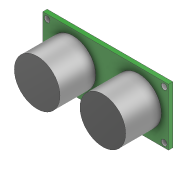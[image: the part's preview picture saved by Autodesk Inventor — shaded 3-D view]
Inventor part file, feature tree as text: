
AUTODESK INVENTOR PART (.ipt)
format: ipt  version: 2022 (Build 260153000, 153)  size: 144,384 bytes
history: native  units: mm
features: sketch x3, extrude x2, hole x1
ambient origin geometry x8: Origin, YZ Plane, XZ Plane, XY Plane, X Axis, Y Axis, Z Axis, Center Point
bodies: Solid1 (feature_tree)
feature tree (6):
  extrude  "Extrusion1"  Depth=20.0mm
  extrude  "Extrusion2"  Depth=1.5mm
  hole  "Hole1"  [1 undecoded]
  sketch  "Sketch1"  dims[d0=44.0mm d1=20.0mm]
  sketch  "Sketch2"  dims[d2=1.5mm d3=0.0mm d4=16.0mm]
  sketch  "Sketch3"  dims[d5=2.5mm d6=12.5mm d7=0.0mm d8=0.5mm d9=0.5mm d10=0.5mm d11=0.5mm d12=2.0mm d13=2.0mm d14=2.0mm d15=2.0mm d16=2.0mm d17=6.0mm d18=4.0mm d19=2.0mm d20=90.0deg d21=6.0mm d22=0.0mm]
note: 1 required parameter value undecoded (feature->parameter linkage not recoverable at this tier; creation-order binding heuristic only, values carry confidence <= 0.55)
